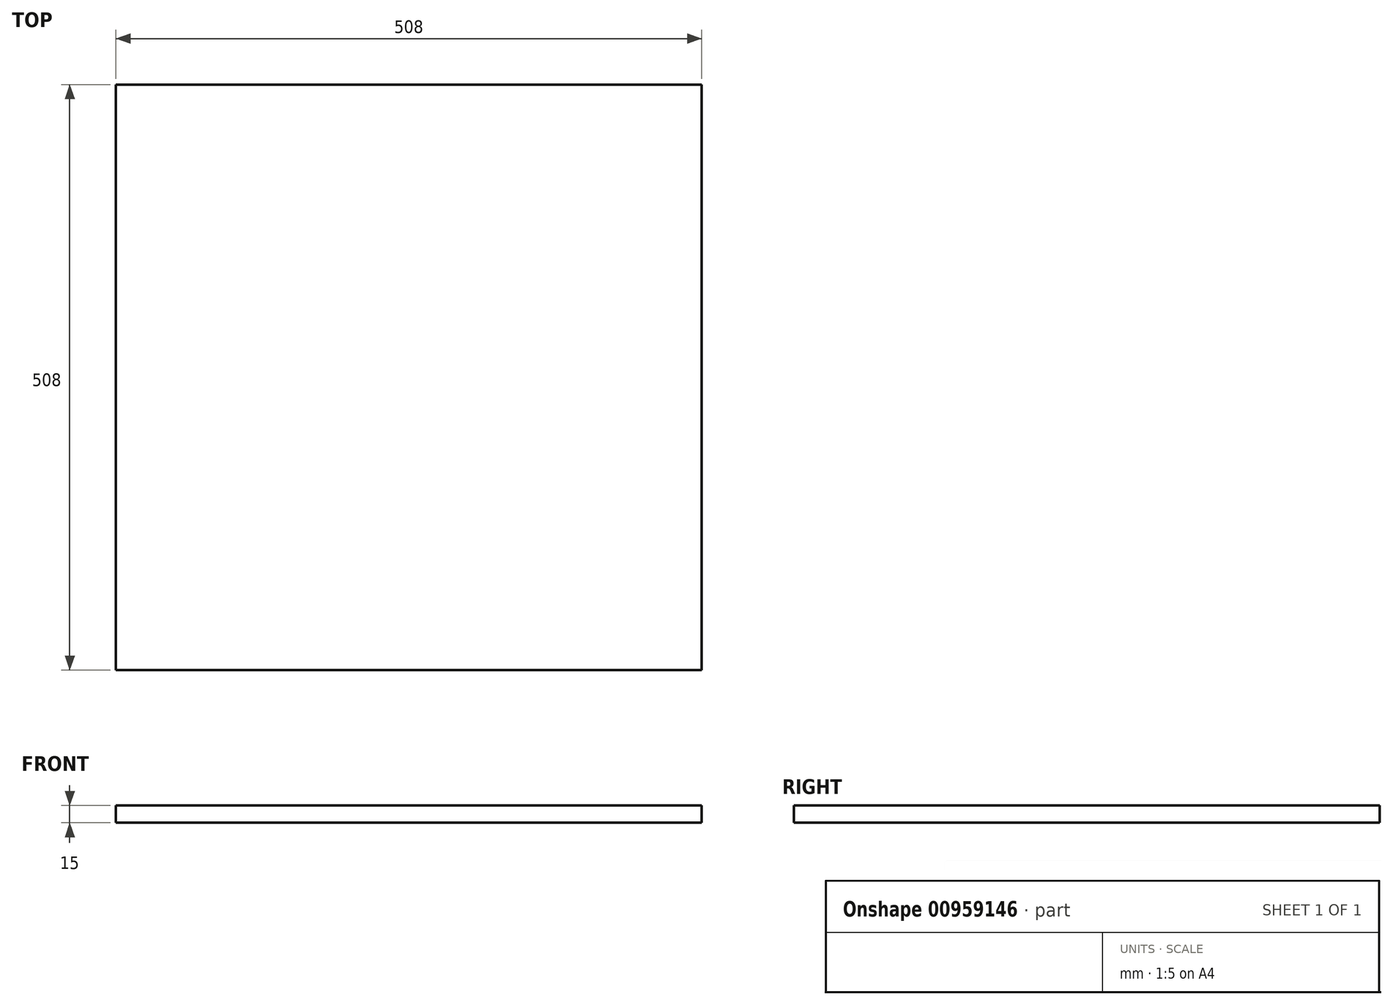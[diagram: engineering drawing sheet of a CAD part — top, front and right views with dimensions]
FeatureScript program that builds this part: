
annotation { "Feature Type Name" : "Feature", "Feature Type Description" : "" }
export const myFeature = defineFeature(function(context is Context, id is Id, definition is map)
    precondition{}
    {
        {
            var Q0;
            Q0=qCreatedBy(makeId("Top.planeOp"),FACE);
            var sketch = newSketch(context, id + "F0", { "sketchPlane" : qUnion([Q0])});
            skLineSegment(sketch, "E0.bottom", {"start": v(254, 254) * mm, "end": v(-254, 254) * mm});
            skLineSegment(sketch, "E0.top", {"start": v(254, -254) * mm, "end": v(-254, -254) * mm});
            skLineSegment(sketch, "E0.left", {"start": v(254, 254) * mm, "end": v(254, -254) * mm});
            skLineSegment(sketch, "E0.right", {"start": v(-254, 254) * mm, "end": v(-254, -254) * mm});
            skPoint(sketch, "E0.middle", {"position": v(0, 0) * mm});
            skSolve(sketch);
        }
        {
            var Q0;
            Q0=makeQuery(id+"F0.imprint","IMPRINT",FACE,{"disambiguationData":[TD([[makeQuery(id+"F0.imprint","IMPRINT",EDGE,{"derivedFrom":sQuery(id+"F0.wireOp",EDGE,"E0.bottom")}),1.0]])]});
            extrude(context, id + "F1", {"entities" : qUnion([Q0]), "depth" : 15 * mm, "offsetDistance" : 25.4 * mm});
        }
    });
